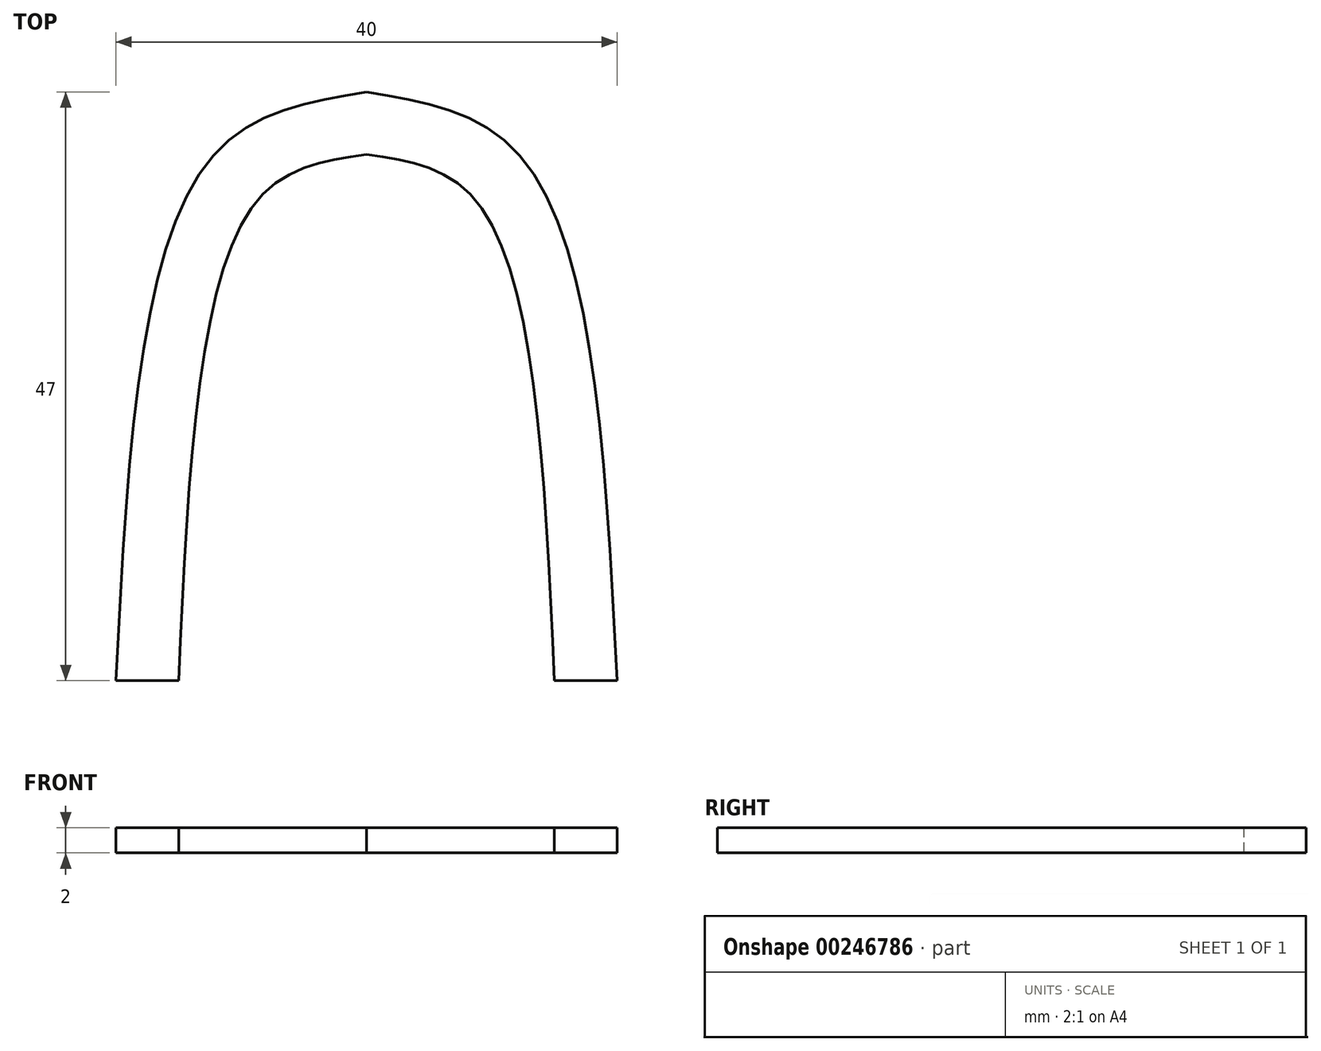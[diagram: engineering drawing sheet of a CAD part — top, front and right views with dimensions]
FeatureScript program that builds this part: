
annotation { "Feature Type Name" : "Feature", "Feature Type Description" : "" }
export const myFeature = defineFeature(function(context is Context, id is Id, definition is map)
    precondition{}
    {
        {
            var Q0;
            Q0=qCreatedBy(makeId("Top.planeOp"),FACE);
            var sketch = newSketch(context, id + "F0", { "sketchPlane" : qUnion([Q0])});
            skLineSegment(sketch, "E0.left", {"start": v(0, 42) * mm, "end": v(0, 47) * mm});
            skPoint(sketch, "E1.visualSharp", {"position": v(15, 0) * mm});
            skFitSpline(sketch, "E2", {"points": [v(0, 42) * mm, v(8.94, 38.06) * mm, v(15, 0) * mm], "startDerivative": vector(29.64, -4.14) * mm, "endDerivative": vector(3.26, -72.35) * mm});
            skLineSegment(sketch, "E3", {"start": v(15, 0) * mm, "end": v(20, 0) * mm});
            skFitSpline(sketch, "E4", {"points": [v(0, 47) * mm, v(12.7, 41.37) * mm, v(20, 0) * mm], "startDerivative": vector(39.01, -6.35) * mm, "endDerivative": vector(4.13, -80.94) * mm});
            skFitSpline(sketch, "E5.MirrorCS", {"points": [v(0, 47) * mm, v(-12.7, 41.37) * mm, v(-20, 0) * mm], "startDerivative": vector(-39.01, -6.35) * mm, "endDerivative": vector(-4.13, -80.94) * mm});
            skFitSpline(sketch, "E6.MirrorCS", {"points": [v(0, 42) * mm, v(-8.94, 38.06) * mm, v(-15, 0) * mm], "startDerivative": vector(-29.64, -4.14) * mm, "endDerivative": vector(-3.26, -72.35) * mm});
            skLineSegment(sketch, "E7.MirrorCS", {"start": v(-15, 0) * mm, "end": v(-20, 0) * mm});
            skSolve(sketch);
        }
        {
            var Q0;
            Q0 = qSketchRegion(id + "F0", true);
            extrude(context, id + "F1", {"entities" : qUnion([Q0]), "depth" : 2 * mm});
        }
    });
